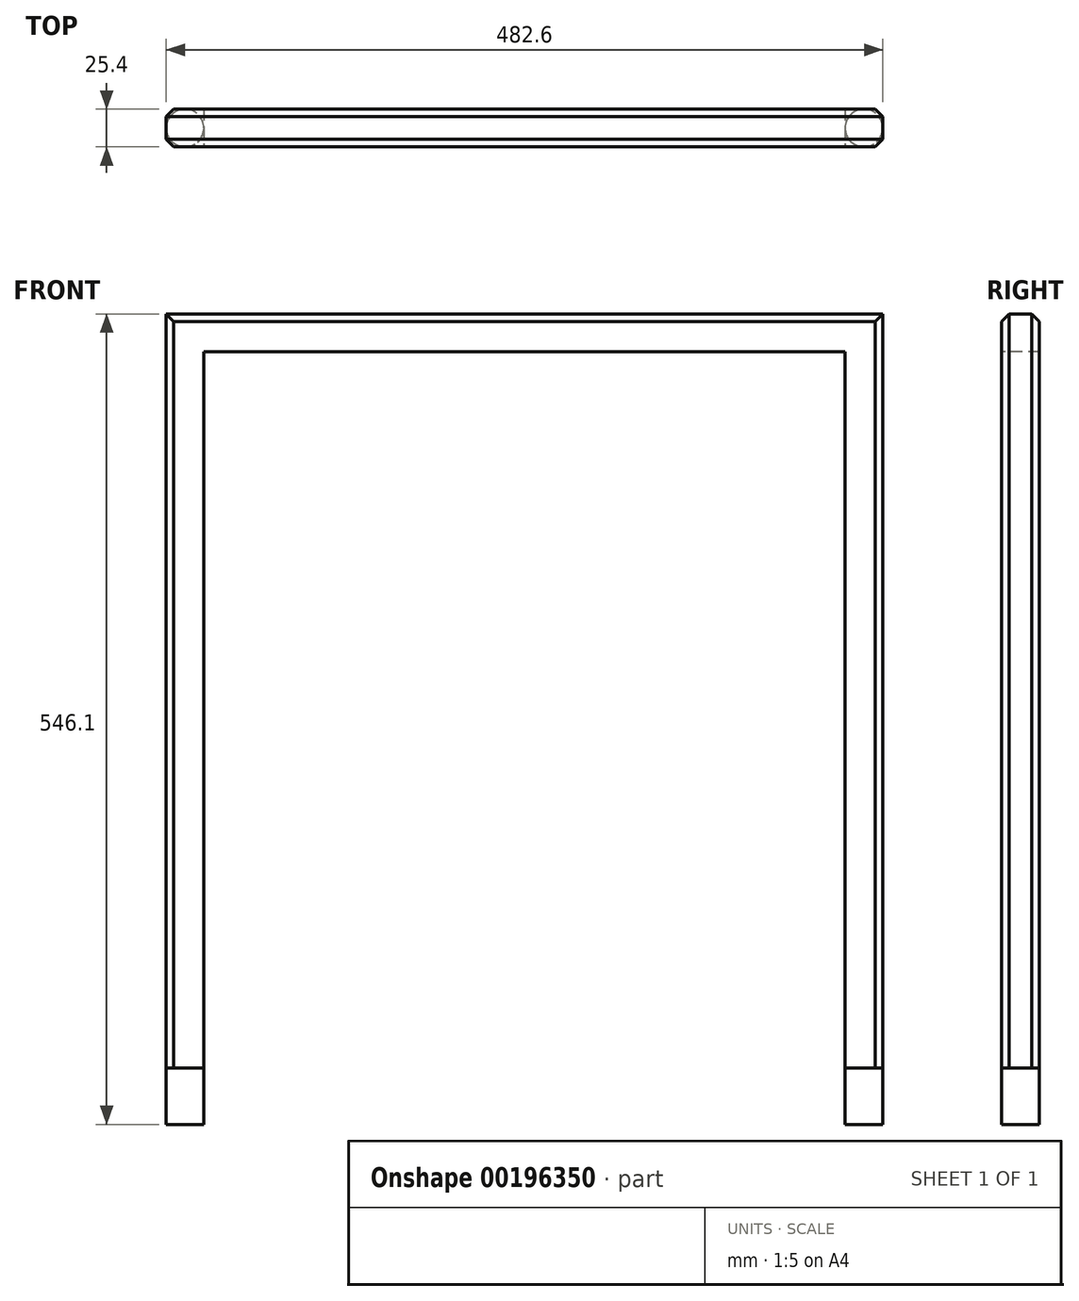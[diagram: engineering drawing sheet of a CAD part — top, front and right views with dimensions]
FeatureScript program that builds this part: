
annotation { "Feature Type Name" : "Feature", "Feature Type Description" : "" }
export const myFeature = defineFeature(function(context is Context, id is Id, definition is map)
    precondition{}
    {
        {
            var Q0;
            Q0=qCreatedBy(makeId("Front.planeOp"),FACE);
            var sketch = newSketch(context, id + "F0", { "sketchPlane" : qUnion([Q0])});
            skLineSegment(sketch, "E0", {"start": v(0, 0) * mm, "end": v(-25.4, 0) * mm});
            skLineSegment(sketch, "E1", {"start": v(-25.4, 0) * mm, "end": v(-25.4, 508) * mm});
            skLineSegment(sketch, "E2", {"start": v(-25.4, 508) * mm, "end": v(457.2, 508) * mm});
            skLineSegment(sketch, "E3", {"start": v(457.2, 508) * mm, "end": v(457.2, 0) * mm});
            skLineSegment(sketch, "E4", {"start": v(457.2, 0) * mm, "end": v(431.8, 0) * mm});
            skLineSegment(sketch, "E5", {"start": v(431.8, 0) * mm, "end": v(431.8, 482.6) * mm});
            skLineSegment(sketch, "E6", {"start": v(431.8, 482.6) * mm, "end": v(0, 482.6) * mm});
            skLineSegment(sketch, "E7", {"start": v(0, 482.6) * mm, "end": v(0, 0) * mm});
            skSolve(sketch);
        }
        {
            var Q0;
            Q0 = qSketchRegion(id + "F0", true);
            extrude(context, id + "F1", {"entities" : qUnion([Q0]), "oppositeDirection" : true, "depth" : 25.4 * mm});
        }
        {
            var Q0;
            Q0=makeQuery(id+"F1.opExtrude","SWEPT_FACE",FACE,{"disambiguationData":[OSD([sQuery(id+"F0.wireOp",EDGE,"E0")])]});
            var sketch = newSketch(context, id + "F2", { "sketchPlane" : qUnion([Q0])});
            skLineSegment(sketch, "E8", {"start": v(-12.7, 0) * mm, "end": v(-12.7, -25.4) * mm});
            skLineSegment(sketch, "E9", {"start": v(-25.4, -12.7) * mm, "end": v(0, -12.7) * mm});
            skCircle(sketch, "E10", {"center": v(-12.7, -12.7) * mm, "radius": 12.7 * mm});
            skLineSegment(sketch, "E11", {"start": v(-12.7, 0) * mm, "end": v(-25.4, 0) * mm});
            skLineSegment(sketch, "E12", {"start": v(-25.4, 0) * mm, "end": v(-25.4, -12.7) * mm});
            skLineSegment(sketch, "E13", {"start": v(-25.4, -12.7) * mm, "end": v(-25.4, -25.4) * mm});
            skLineSegment(sketch, "E14", {"start": v(-25.4, -25.4) * mm, "end": v(-12.7, -25.4) * mm});
            skLineSegment(sketch, "E15", {"start": v(-12.7, -25.4) * mm, "end": v(0, -25.4) * mm});
            skLineSegment(sketch, "E16", {"start": v(0, -25.4) * mm, "end": v(0, -12.7) * mm});
            skLineSegment(sketch, "E17", {"start": v(0, -12.7) * mm, "end": v(0, 0) * mm});
            skLineSegment(sketch, "E18", {"start": v(0, 0) * mm, "end": v(-12.7, 0) * mm});
            skSolve(sketch);
        }
        {
            var Q0;
            {var subQ1=sQuery(id+"F2.wireOp",EDGE,"E8");var subQ3=sQuery(id+"F2.wireOp",EDGE,"E9");var subQ4=makeQuery(id+"F2.imprint","INTERSECT",VERTEX,{"derivedFrom":[subQ1,subQ3]});Q0=makeQuery(id+"F2.imprint","IMPRINT",FACE,{"disambiguationData":[TD([[makeQuery(id+"F2.imprint","IMPRINT",EDGE,{"disambiguationData":[TD([[subQ4,1.0]])],"derivedFrom":subQ1}),-1.0]])]});}
            var Q1;
            {var subQ1=sQuery(id+"F2.wireOp",EDGE,"E8");var subQ3=sQuery(id+"F2.wireOp",EDGE,"E9");var subQ4=makeQuery(id+"F2.imprint","INTERSECT",VERTEX,{"derivedFrom":[subQ1,subQ3]});Q1=makeQuery(id+"F2.imprint","IMPRINT",FACE,{"disambiguationData":[TD([[makeQuery(id+"F2.imprint","IMPRINT",EDGE,{"disambiguationData":[TD([[subQ4,1.0]])],"derivedFrom":subQ1}),1.0]])]});}
            var Q2;
            {var subQ1=sQuery(id+"F2.wireOp",EDGE,"E8");var subQ3=sQuery(id+"F2.wireOp",EDGE,"E9");var subQ4=makeQuery(id+"F2.imprint","INTERSECT",VERTEX,{"derivedFrom":[subQ1,subQ3]});Q2=makeQuery(id+"F2.imprint","IMPRINT",FACE,{"disambiguationData":[TD([[makeQuery(id+"F2.imprint","IMPRINT",EDGE,{"disambiguationData":[TD([[subQ4,-1.0]])],"derivedFrom":subQ1}),-1.0]])]});}
            var Q3;
            {var subQ1=sQuery(id+"F2.wireOp",EDGE,"E8");var subQ3=sQuery(id+"F2.wireOp",EDGE,"E9");var subQ4=makeQuery(id+"F2.imprint","INTERSECT",VERTEX,{"derivedFrom":[subQ1,subQ3]});Q3=makeQuery(id+"F2.imprint","IMPRINT",FACE,{"disambiguationData":[TD([[makeQuery(id+"F2.imprint","IMPRINT",EDGE,{"disambiguationData":[TD([[subQ4,-1.0]])],"derivedFrom":subQ1}),1.0]])]});}
            extrude(context, id + "F3", {"entities" : qUnion([Q0, Q1, Q2, Q3]), "operationType" : NewBodyOperationType.ADD, "depth" : 38.1 * mm});
        }
        {
            var Q0;
            Q0=makeQuery(id+"F1.opExtrude","SWEPT_FACE",FACE,{"disambiguationData":[OSD([sQuery(id+"F0.wireOp",EDGE,"E4")])]});
            var sketch = newSketch(context, id + "F4", { "sketchPlane" : qUnion([Q0])});
            skLineSegment(sketch, "E19", {"start": v(431.8, -12.7) * mm, "end": v(457.2, -12.7) * mm});
            skLineSegment(sketch, "E20", {"start": v(444.5, -25.4) * mm, "end": v(444.5, 0) * mm});
            skCircle(sketch, "E21", {"center": v(444.5, -12.7) * mm, "radius": 12.7 * mm});
            skLineSegment(sketch, "E22", {"start": v(457.2, -12.7) * mm, "end": v(457.2, 0) * mm});
            skLineSegment(sketch, "E23", {"start": v(457.2, 0) * mm, "end": v(444.5, 0) * mm});
            skLineSegment(sketch, "E24", {"start": v(444.5, 0) * mm, "end": v(431.8, 0) * mm});
            skLineSegment(sketch, "E25", {"start": v(431.8, 0) * mm, "end": v(431.8, -12.7) * mm});
            skLineSegment(sketch, "E26", {"start": v(431.8, -12.7) * mm, "end": v(431.8, -25.4) * mm});
            skLineSegment(sketch, "E27", {"start": v(431.8, -25.4) * mm, "end": v(444.5, -25.4) * mm});
            skSolve(sketch);
        }
        {
            var Q0;
            {var subQ1=sQuery(id+"F4.wireOp",EDGE,"E19");var subQ3=sQuery(id+"F4.wireOp",EDGE,"E20");var subQ4=makeQuery(id+"F4.imprint","INTERSECT",VERTEX,{"derivedFrom":[subQ1,subQ3]});Q0=makeQuery(id+"F4.imprint","IMPRINT",FACE,{"disambiguationData":[TD([[makeQuery(id+"F4.imprint","IMPRINT",EDGE,{"disambiguationData":[TD([[subQ4,1.0]])],"derivedFrom":subQ1}),-1.0]])]});}
            var Q1;
            {var subQ1=sQuery(id+"F4.wireOp",EDGE,"E19");var subQ3=sQuery(id+"F4.wireOp",EDGE,"E20");var subQ4=makeQuery(id+"F4.imprint","INTERSECT",VERTEX,{"derivedFrom":[subQ1,subQ3]});Q1=makeQuery(id+"F4.imprint","IMPRINT",FACE,{"disambiguationData":[TD([[makeQuery(id+"F4.imprint","IMPRINT",EDGE,{"disambiguationData":[TD([[subQ4,1.0]])],"derivedFrom":subQ1}),1.0]])]});}
            var Q2;
            {var subQ1=sQuery(id+"F4.wireOp",EDGE,"E19");var subQ4=sQuery(id+"F4.wireOp",EDGE,"E20");var subQ5=makeQuery(id+"F4.imprint","INTERSECT",VERTEX,{"derivedFrom":[subQ1,subQ4]});Q2=makeQuery(id+"F4.imprint","IMPRINT",FACE,{"disambiguationData":[TD([[makeQuery(id+"F4.imprint","IMPRINT",EDGE,{"disambiguationData":[TD([[subQ5,1.0]])],"derivedFrom":subQ4}),-1.0]])]});}
            var Q3;
            {var subQ1=sQuery(id+"F4.wireOp",EDGE,"E19");var subQ3=sQuery(id+"F4.wireOp",EDGE,"E20");var subQ4=makeQuery(id+"F4.imprint","INTERSECT",VERTEX,{"derivedFrom":[subQ1,subQ3]});Q3=makeQuery(id+"F4.imprint","IMPRINT",FACE,{"disambiguationData":[TD([[makeQuery(id+"F4.imprint","IMPRINT",EDGE,{"disambiguationData":[TD([[subQ4,-1.0]])],"derivedFrom":subQ3}),-1.0]])]});}
            extrude(context, id + "F5", {"entities" : qUnion([Q0, Q1, Q2, Q3]), "operationType" : NewBodyOperationType.ADD, "depth" : 38.1 * mm});
        }
        {
            var Q0;
            Q0=makeQuery(id+"F1.opExtrude","CAP_EDGE",EDGE,{"disambiguationData":[OSD([sQuery(id+"F0.wireOp",EDGE,"E3")])],"isStart":false});
            var Q1;
            Q1=makeQuery(id+"F1.opExtrude","CAP_EDGE",EDGE,{"disambiguationData":[OSD([sQuery(id+"F0.wireOp",EDGE,"E3")])],"isStart":true});
            var Q2;
            Q2=makeQuery(id+"F1.opExtrude","CAP_EDGE",EDGE,{"disambiguationData":[OSD([sQuery(id+"F0.wireOp",EDGE,"E1")])],"isStart":false});
            var Q3;
            Q3=makeQuery(id+"F1.opExtrude","CAP_EDGE",EDGE,{"disambiguationData":[OSD([sQuery(id+"F0.wireOp",EDGE,"E1")])],"isStart":true});
            var Q4;
            Q4=makeQuery(id+"F1.opExtrude","CAP_EDGE",EDGE,{"disambiguationData":[OSD([sQuery(id+"F0.wireOp",EDGE,"E2")])],"isStart":true});
            var Q5;
            Q5=makeQuery(id+"F1.opExtrude","CAP_EDGE",EDGE,{"disambiguationData":[OSD([sQuery(id+"F0.wireOp",EDGE,"E2")])],"isStart":false});
            chamfer(context, id + "F6", {"entities" : qUnion([Q0, Q1, Q2, Q3, Q4, Q5]), "width" : 5.08 * mm, "tangentPropagation" : true});
        }
    });
